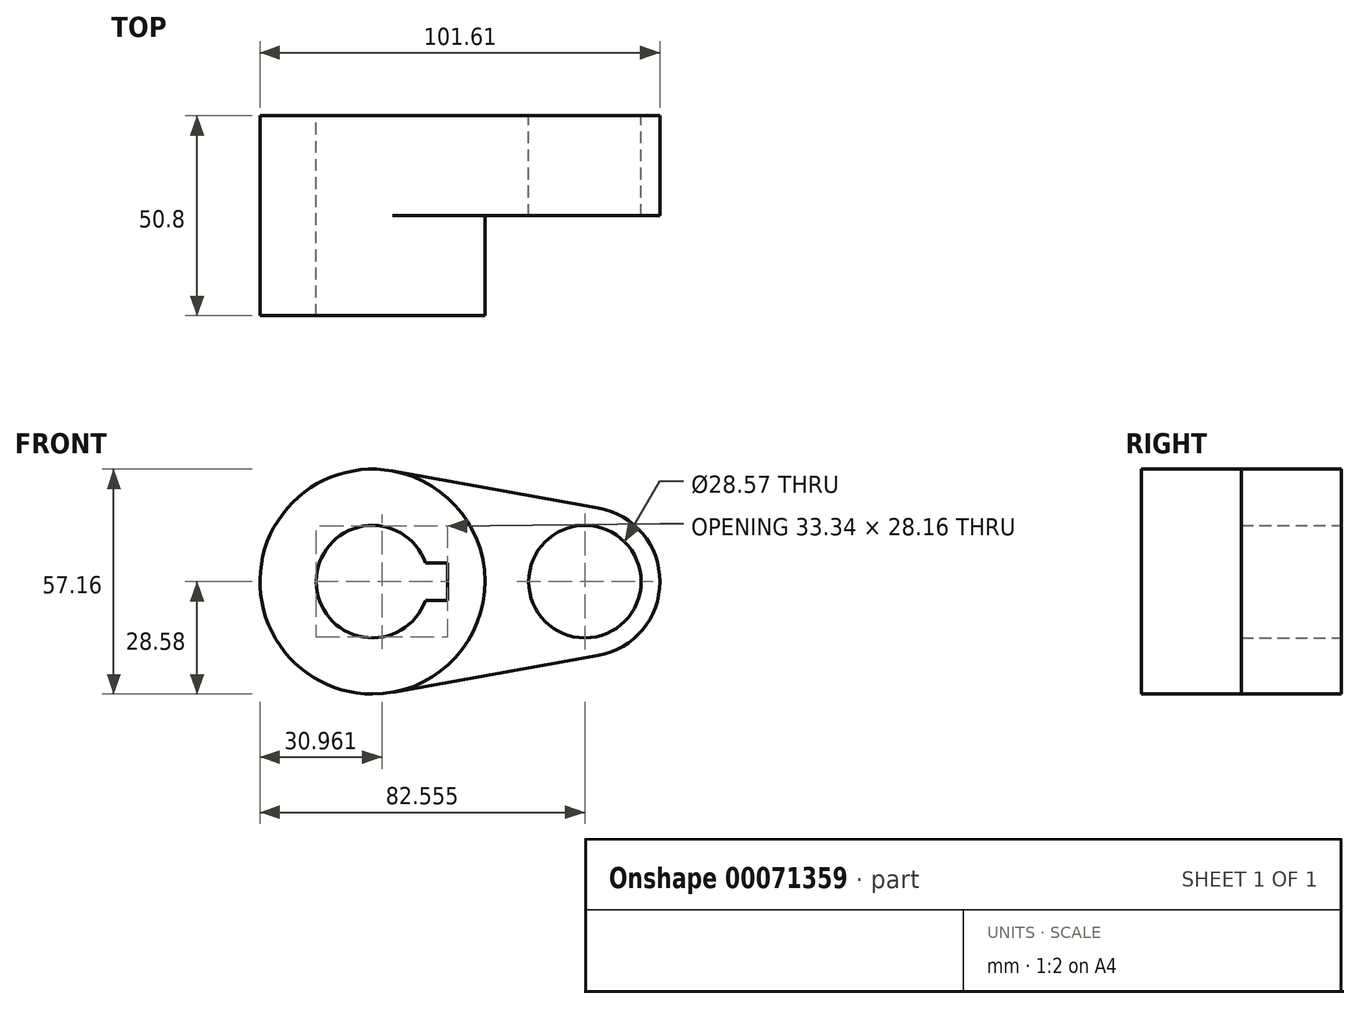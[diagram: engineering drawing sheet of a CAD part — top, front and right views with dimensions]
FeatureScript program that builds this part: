
annotation { "Feature Type Name" : "Feature", "Feature Type Description" : "" }
export const myFeature = defineFeature(function(context is Context, id is Id, definition is map)
    precondition{}
    {
        {
            var Q0;
            Q0=qCreatedBy(makeId("Front.planeOp"),FACE);
            var sketch = newSketch(context, id + "F0", { "sketchPlane" : qUnion([Q0])});
            skCircle(sketch, "E0", {"center": v(0, 0) * mm, "radius": 28.58 * mm});
            skCircle(sketch, "E1", {"center": v(53.97, 0) * mm, "radius": 19.05 * mm});
            skLineSegment(sketch, "E2", {"start": v(5.04, -28.13) * mm, "end": v(57.34, -18.75) * mm});
            skCircle(sketch, "E3", {"center": v(0, 0) * mm, "radius": 14.29 * mm});
            skCircle(sketch, "E4", {"center": v(53.97, 0) * mm, "radius": 14.29 * mm});
            skLineSegment(sketch, "E5", {"start": v(5.04, 28.13) * mm, "end": v(57.34, 18.75) * mm});
            skLineSegment(sketch, "E6.rect.bottom", {"start": v(19.05, 4.76) * mm, "end": v(-19.05, 4.76) * mm});
            skLineSegment(sketch, "E6.rect.top", {"start": v(19.05, -4.76) * mm, "end": v(-19.05, -4.76) * mm});
            skLineSegment(sketch, "E6.rect.left", {"start": v(19.05, 4.76) * mm, "end": v(19.05, -4.76) * mm});
            skLineSegment(sketch, "E6.rect.right", {"start": v(-19.05, 4.76) * mm, "end": v(-19.05, -4.76) * mm});
            skSolve(sketch);
        }
        {
            var Q0;
            {var subQ4=sQuery(id+"F0.wireOp",EDGE,"E6.rect.left");Q0=makeQuery(id+"F0.imprint","IMPRINT",FACE,{"disambiguationData":[TD([[makeQuery(id+"F0.imprint","IMPRINT",EDGE,{"derivedFrom":subQ4}),1.0]])]});}
            var Q1;
            {var subQ0=sQuery(id+"F0.wireOp",EDGE,"E2");Q1=makeQuery(id+"F0.imprint","IMPRINT",FACE,{"disambiguationData":[TD([[makeQuery(id+"F0.imprint","IMPRINT",EDGE,{"derivedFrom":subQ0}),1.0]])]});}
            var Q2;
            Q2=makeQuery(id+"F0.imprint","IMPRINT",FACE,{"disambiguationData":[TD([[makeQuery(id+"F0.imprint","IMPRINT",EDGE,{"derivedFrom":sQuery(id+"F0.wireOp",EDGE,"E4")}),-1.0]])]});
            extrude(context, id + "F1", {"entities" : qUnion([Q0, Q1, Q2]), "depth" : 25.4 * mm});
        }
        {
            var Q0;
            {var subQ4=sQuery(id+"F0.wireOp",EDGE,"E6.rect.left");Q0=makeQuery(id+"F0.imprint","IMPRINT",FACE,{"disambiguationData":[TD([[makeQuery(id+"F0.imprint","IMPRINT",EDGE,{"derivedFrom":subQ4}),1.0]])]});}
            var Q1;
            {var subQ5=sQuery(id+"F0.wireOp",EDGE,"E6.rect.right");Q1=makeQuery(id+"F0.imprint","IMPRINT",FACE,{"disambiguationData":[TD([[makeQuery(id+"F0.imprint","IMPRINT",EDGE,{"derivedFrom":subQ5}),1.0]])]});}
            extrude(context, id + "F2", {"entities" : qUnion([Q0, Q1]), "operationType" : NewBodyOperationType.ADD, "depth" : 50.8 * mm});
        }
    });
